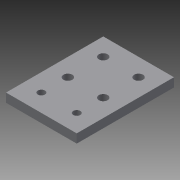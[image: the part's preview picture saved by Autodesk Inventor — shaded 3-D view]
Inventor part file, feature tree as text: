
AUTODESK INVENTOR PART (.ipt)
format: ipt  version: 2013 (Build 170138000, 138)  size: 98,816 bytes
history: native  units: in
note: dims shown in document units (in); Inventor stores cm internally (conversion verified against a paired STEP export)
features: extrude x1, sketch x1
ambient origin geometry x8: Origin, YZ Plane, XZ Plane, XY Plane, X Axis, Y Axis, Z Axis, Center Point
bodies: Solid1 (feature_tree)
feature tree (2):
  extrude  "Extrusion1"  Depth=2.75in
  sketch  "Sketch1"  dims[d0=2.0in d1=2.75in d2=0.5in d3=0.5in d4=0.5in d5=0.5in d6=1.0in d7=90.0deg d8=1.0in d13=0.2in d14=0.2in d15=0.25in d16=0.25in d17=0.25in d18=0.25in d19=0.25in d20=0.0in]
